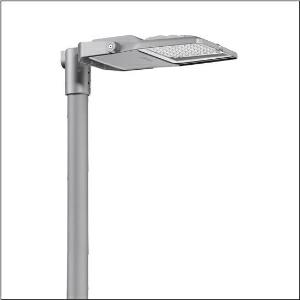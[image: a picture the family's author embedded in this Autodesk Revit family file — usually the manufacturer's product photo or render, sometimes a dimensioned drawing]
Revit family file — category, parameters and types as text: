
# Revit family: floodlight_fl_21_iq_mini___pl33t_5xa7771c4f3a_1d16
name_source: partatom
category: Lighting Fixtures
units: mm (PartAtom-declared; Revit-internal decimal feet)

## family parameters
Cut with Voids When Loaded = No
Host = Face
Light Source = No
Part Type = Normal
Room Calculation Point = No
Round Connector Dimension = Use Diameter
Shared = No

## types (1)
- --- (1 x LED, 12570 lm, 87.2 W, 4000K)
    Apparent Load = 87 VA
    CIE Flux Codes = 26 75 99 100 100
    Color Rendering = 70
    Color Temperature = 4000K
    Default Elevation = 1800 mm
    Description = Floodlight FL 21 iQ mini, floodlight, primary light control with lens, of PMMA, primary optical cover: protective disc, of toughened safety glass, transparent, light distribution: PL33T, light emission: direct distribution, installation type: surface-mounted, LED, High Power LED, rated luminous flux: 12.570lm, luminous efficacy: 144lm/W, light colour: 740, colour temperature: 4000K, control: Auto-Match, Temp-Guard, Lumen-Switch, Night-Set, Smart-Wire, Light-Fading, Desk-Remote (wireless, voltage-free reading and setting of iQ features in the workshop via application-optimized NFC function/RFID function), optimised constant luminous flux control (CLO 2.0), with terminal, 6-pole, mains connection: 220..240V, AC, 50/60Hz, start of lifetime: 87W, end of service life: 92W, reduction: 40W, luminaire housing, of diecast aluminium, powder-coated, Siteco® metallic grey (DB 702S), corrosivity category C5 mid according to DIN EN ISO 12944, sealing non-destructively replaceable, please order mast flange separately, mast bracket, of steel, galvanised, powder-coated, Siteco® metallic grey (DB 702S), protection rating (complete): IP66, insulation class (complete): insulation class II (safety insulation), certification: CE, ENEC, VDE, protection symbol: D, impact resistance: IK08, permissible operating ambient temperature: -40..+40°C, permissible operating ambient temperature for outdoor applications: -40..+50°C, standard: DIN EN 12944, LABS conformity tested according to VDMA 24364:2018-05, packaging unit: 1 piece

Light Distribution: PL33T
    Height = 70 mm
    Lamp = 1 x LED
    Lamp Light Flux = 12570 lm
    Lamp Power = 87.2 W
    Lamp count = 1
    Length = 485 mm
    Luminous efficacy = 144 lm/W
    Manufacturer = Siteco
    ModVariant = No
    Model = 5XA7771C4F3A
    Number of Poles = 1
    OnlyDefault = Yes
    Power Factor = 1
    Product Name = Floodlight FL 21 iQ mini | PL33T
    Product group = floodlight | pylon annexe
    ProductGroupID = 6200
    Protection Class = Protection class II
    Protection Degree = IP 66
    RLX_Detail_Level = 1
    RLX_Emergency_Light_Flux = 0 lm
    RLX_Emergency_Type = 0
    RLX_Emergency_Type_DB = No
    RlxData = <blob elided: 101237 chars, md5=589ce00f>
    Socket = socket
    Standby Power = 0 W
    System Light Flux = 12570 lm
    System Power = 87 W
    Type Comments = factory setting: luminous flux: 100 % | dim-lin: 254 | 456 mA
    Type Image = l_1007125.jpg
    URL = http://relux.com
    VarID = @adj_099793
    Voltage = 0 V
    Weight = 0.00 kg
    Width = 337 mm

## geometry (parser evidence)
native form markers: Blend x4, Sweep x12
no freeform markers — native parametric forms only
